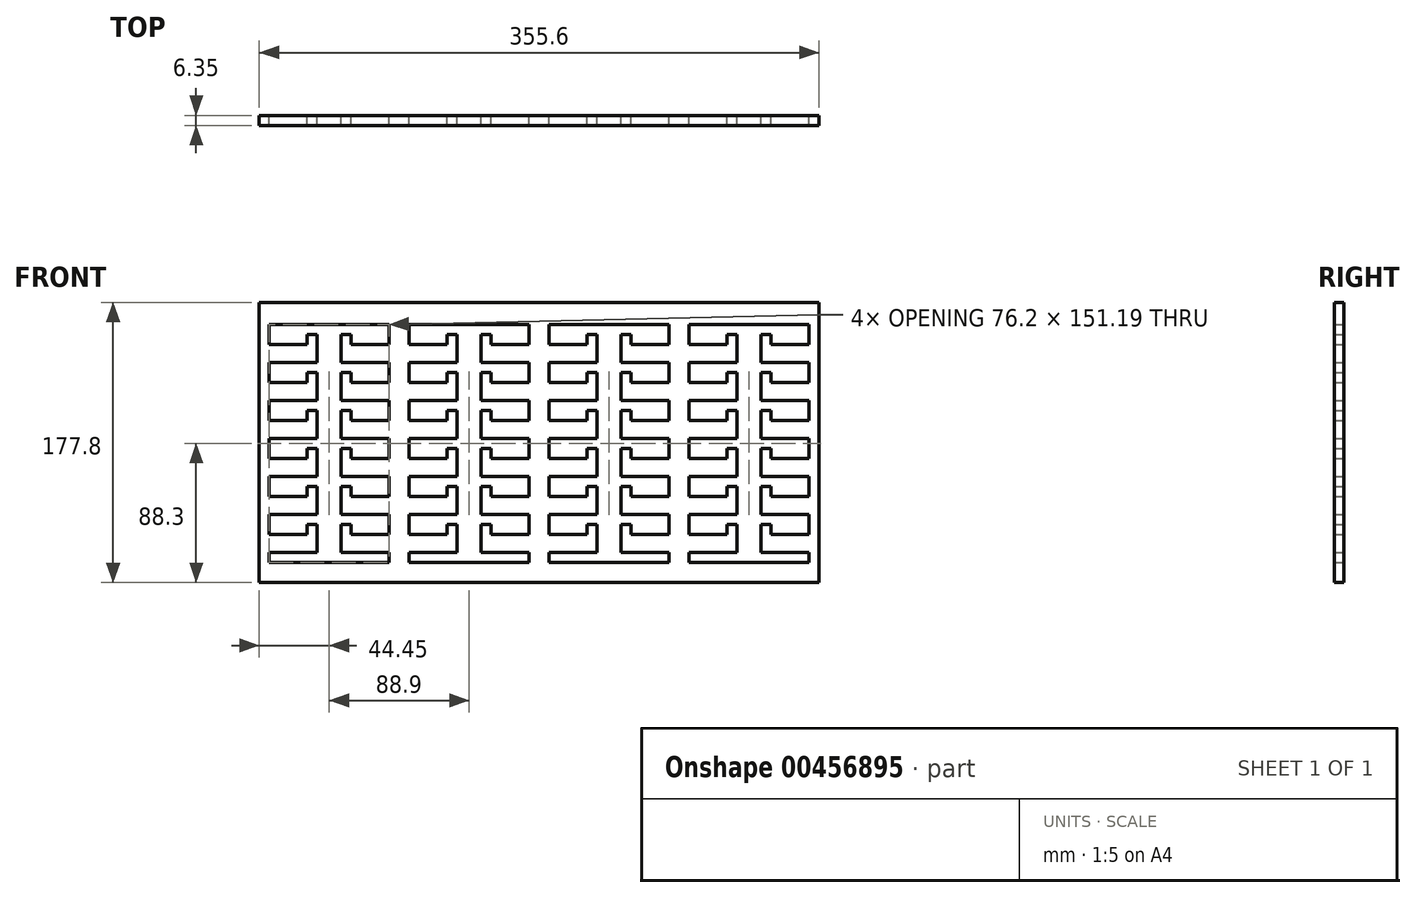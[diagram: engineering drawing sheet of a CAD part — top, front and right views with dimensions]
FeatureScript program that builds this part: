
annotation { "Feature Type Name" : "Feature", "Feature Type Description" : "" }
export const myFeature = defineFeature(function(context is Context, id is Id, definition is map)
    precondition{}
    {
        {
            var Q0;
            Q0=qCreatedBy(makeId("Front.planeOp"),FACE);
            var sketch = newSketch(context, id + "F0", { "sketchPlane" : qUnion([Q0])});
            skLineSegment(sketch, "E0", {"start": v(-97.96, -49.5) * mm, "end": v(-67.48, -49.5) * mm});
            skLineSegment(sketch, "E1", {"start": v(-67.48, -49.5) * mm, "end": v(-67.48, -31.72) * mm});
            skLineSegment(sketch, "E2", {"start": v(-67.48, -31.72) * mm, "end": v(-73.83, -31.72) * mm});
            skLineSegment(sketch, "E3", {"start": v(-73.83, -31.72) * mm, "end": v(-73.83, -38.07) * mm});
            skLineSegment(sketch, "E4", {"start": v(-73.83, -38.07) * mm, "end": v(-97.96, -38.07) * mm});
            skLineSegment(sketch, "E5", {"start": v(-97.96, -38.07) * mm, "end": v(-97.96, -25.37) * mm});
            skLineSegment(sketch, "E6", {"start": v(-97.96, -25.37) * mm, "end": v(-67.48, -25.37) * mm});
            skLineSegment(sketch, "E7", {"start": v(-67.48, -25.37) * mm, "end": v(-67.48, -7.6) * mm});
            skLineSegment(sketch, "E8", {"start": v(-67.48, -7.6) * mm, "end": v(-73.83, -7.6) * mm});
            skLineSegment(sketch, "E9", {"start": v(-73.83, -7.6) * mm, "end": v(-73.83, -13.94) * mm});
            skLineSegment(sketch, "E10", {"start": v(-73.83, -13.94) * mm, "end": v(-97.96, -13.94) * mm});
            skLineSegment(sketch, "E11", {"start": v(-97.96, -13.94) * mm, "end": v(-97.96, -1.24) * mm});
            skLineSegment(sketch, "E12", {"start": v(-97.96, -1.24) * mm, "end": v(-67.48, -1.24) * mm});
            skLineSegment(sketch, "E13", {"start": v(-67.48, -1.24) * mm, "end": v(-67.48, 16.54) * mm});
            skLineSegment(sketch, "E14", {"start": v(-67.48, 16.54) * mm, "end": v(-73.83, 16.54) * mm});
            skLineSegment(sketch, "E15", {"start": v(-73.83, 16.54) * mm, "end": v(-73.83, 10.19) * mm});
            skLineSegment(sketch, "E16", {"start": v(-73.83, 10.19) * mm, "end": v(-97.96, 10.19) * mm});
            skLineSegment(sketch, "E17", {"start": v(-97.96, 10.19) * mm, "end": v(-97.96, 22.89) * mm});
            skLineSegment(sketch, "E18", {"start": v(-97.96, 22.89) * mm, "end": v(-67.48, 22.89) * mm});
            skLineSegment(sketch, "E19", {"start": v(-67.48, 22.89) * mm, "end": v(-67.48, 40.67) * mm});
            skLineSegment(sketch, "E20", {"start": v(-67.48, 40.67) * mm, "end": v(-73.83, 40.67) * mm});
            skLineSegment(sketch, "E21", {"start": v(-73.83, 40.67) * mm, "end": v(-73.83, 34.32) * mm});
            skLineSegment(sketch, "E22", {"start": v(-73.83, 34.32) * mm, "end": v(-97.96, 34.32) * mm});
            skLineSegment(sketch, "E23", {"start": v(-97.96, 34.32) * mm, "end": v(-97.96, 47.02) * mm});
            skLineSegment(sketch, "E24", {"start": v(-97.96, 47.02) * mm, "end": v(-67.48, 47.02) * mm});
            skLineSegment(sketch, "E25", {"start": v(-67.48, 64.8) * mm, "end": v(-73.83, 64.8) * mm});
            skLineSegment(sketch, "E26", {"start": v(-73.83, 64.8) * mm, "end": v(-73.83, 58.45) * mm});
            skLineSegment(sketch, "E27", {"start": v(-73.83, 58.45) * mm, "end": v(-97.96, 58.45) * mm});
            skLineSegment(sketch, "E28", {"start": v(-97.96, 58.45) * mm, "end": v(-97.96, 71.15) * mm});
            skLineSegment(sketch, "E29", {"start": v(-21.76, -80.05) * mm, "end": v(-21.76, -73.63) * mm});
            skLineSegment(sketch, "E30", {"start": v(-21.76, -73.63) * mm, "end": v(-52.24, -73.63) * mm});
            skLineSegment(sketch, "E31", {"start": v(-52.24, -73.63) * mm, "end": v(-52.24, -55.85) * mm});
            skLineSegment(sketch, "E32", {"start": v(-52.24, -55.85) * mm, "end": v(-45.89, -55.85) * mm});
            skLineSegment(sketch, "E33", {"start": v(-45.89, -55.85) * mm, "end": v(-45.89, -62.2) * mm});
            skLineSegment(sketch, "E34", {"start": v(-45.89, -62.2) * mm, "end": v(-21.76, -62.2) * mm});
            skLineSegment(sketch, "E35", {"start": v(-21.76, -62.2) * mm, "end": v(-21.76, -49.5) * mm});
            skLineSegment(sketch, "E36", {"start": v(-21.76, -49.5) * mm, "end": v(-52.24, -49.5) * mm});
            skLineSegment(sketch, "E37", {"start": v(-52.24, -49.5) * mm, "end": v(-52.24, -31.72) * mm});
            skLineSegment(sketch, "E38", {"start": v(-52.24, -31.72) * mm, "end": v(-45.89, -31.72) * mm});
            skLineSegment(sketch, "E39", {"start": v(-45.89, -31.72) * mm, "end": v(-45.89, -38.07) * mm});
            skLineSegment(sketch, "E40", {"start": v(-45.89, -38.07) * mm, "end": v(-21.76, -38.07) * mm});
            skLineSegment(sketch, "E41", {"start": v(-21.76, -38.07) * mm, "end": v(-21.76, -25.37) * mm});
            skLineSegment(sketch, "E42", {"start": v(-21.76, -25.37) * mm, "end": v(-52.24, -25.37) * mm});
            skLineSegment(sketch, "E43", {"start": v(-52.24, -25.37) * mm, "end": v(-52.24, -7.6) * mm});
            skLineSegment(sketch, "E44", {"start": v(-52.24, -7.6) * mm, "end": v(-45.89, -7.6) * mm});
            skLineSegment(sketch, "E45", {"start": v(-45.89, -7.6) * mm, "end": v(-45.89, -13.94) * mm});
            skLineSegment(sketch, "E46", {"start": v(-45.89, -13.94) * mm, "end": v(-21.76, -13.94) * mm});
            skLineSegment(sketch, "E47", {"start": v(-21.76, -13.94) * mm, "end": v(-21.76, -1.24) * mm});
            skLineSegment(sketch, "E48", {"start": v(-21.76, -1.24) * mm, "end": v(-52.24, -1.24) * mm});
            skLineSegment(sketch, "E49", {"start": v(-52.24, -1.24) * mm, "end": v(-52.24, 16.54) * mm});
            skLineSegment(sketch, "E50", {"start": v(-52.24, 16.54) * mm, "end": v(-45.89, 16.54) * mm});
            skLineSegment(sketch, "E51", {"start": v(-45.89, 16.54) * mm, "end": v(-45.89, 10.19) * mm});
            skLineSegment(sketch, "E52", {"start": v(-45.89, 10.19) * mm, "end": v(-21.76, 10.19) * mm});
            skLineSegment(sketch, "E53", {"start": v(-21.76, 10.19) * mm, "end": v(-21.76, 22.89) * mm});
            skLineSegment(sketch, "E54", {"start": v(-21.76, 22.89) * mm, "end": v(-52.24, 22.89) * mm});
            skLineSegment(sketch, "E55", {"start": v(-52.24, 22.89) * mm, "end": v(-52.24, 40.67) * mm});
            skLineSegment(sketch, "E56", {"start": v(-52.24, 40.67) * mm, "end": v(-45.89, 40.67) * mm});
            skLineSegment(sketch, "E57", {"start": v(-45.89, 40.67) * mm, "end": v(-45.89, 34.32) * mm});
            skLineSegment(sketch, "E58", {"start": v(-45.89, 34.32) * mm, "end": v(-21.76, 34.32) * mm});
            skLineSegment(sketch, "E59", {"start": v(-21.76, 34.32) * mm, "end": v(-21.76, 47.02) * mm});
            skLineSegment(sketch, "E60", {"start": v(-21.76, 47.02) * mm, "end": v(-52.24, 47.02) * mm});
            skLineSegment(sketch, "E61", {"start": v(-52.24, 47.02) * mm, "end": v(-52.24, 64.8) * mm});
            skLineSegment(sketch, "E62", {"start": v(-52.24, 64.8) * mm, "end": v(-45.89, 64.8) * mm});
            skLineSegment(sketch, "E63", {"start": v(-45.89, 64.8) * mm, "end": v(-45.89, 58.45) * mm});
            skLineSegment(sketch, "E64", {"start": v(-45.89, 58.45) * mm, "end": v(-21.76, 58.45) * mm});
            skLineSegment(sketch, "E65", {"start": v(-21.76, 58.45) * mm, "end": v(-21.76, 71.15) * mm});
            skLineSegment(sketch, "E66", {"start": v(-67.48, 47.02) * mm, "end": v(-67.48, 64.8) * mm});
            skLineSegment(sketch, "E67", {"start": v(-67.48, -73.63) * mm, "end": v(-67.48, -55.85) * mm});
            skLineSegment(sketch, "E68", {"start": v(-73.83, -62.2) * mm, "end": v(-73.83, -55.85) * mm});
            skLineSegment(sketch, "E69", {"start": v(-73.83, -55.85) * mm, "end": v(-67.48, -55.85) * mm});
            skLineSegment(sketch, "E70", {"start": v(-67.48, -73.63) * mm, "end": v(-97.96, -73.63) * mm});
            skLineSegment(sketch, "E71", {"start": v(-97.96, -62.2) * mm, "end": v(-97.96, -49.5) * mm});
            skLineSegment(sketch, "E72", {"start": v(-97.96, -73.63) * mm, "end": v(-97.96, -80.05) * mm});
            skLineSegment(sketch, "E73", {"start": v(-97.96, -62.2) * mm, "end": v(-73.83, -62.2) * mm});
            skLineSegment(sketch, "E74", {"start": v(-97.96, -80.05) * mm, "end": v(-21.76, -80.05) * mm});
            skLineSegment(sketch, "E75", {"start": v(-97.96, 71.15) * mm, "end": v(-21.76, 71.15) * mm});
            skPoint(sketch, "E76", {"position": v(-59.86, 71.15) * mm});
            skPoint(sketch, "E77", {"position": v(-59.86, -80.05) * mm});
            skLineSegment(sketch, "E78", {"start": v(-186.86, -49.5) * mm, "end": v(-156.38, -49.5) * mm});
            skLineSegment(sketch, "E79", {"start": v(-156.38, -49.5) * mm, "end": v(-156.38, -31.72) * mm});
            skLineSegment(sketch, "E80", {"start": v(-156.38, -31.72) * mm, "end": v(-162.73, -31.72) * mm});
            skLineSegment(sketch, "E81", {"start": v(-162.73, -31.72) * mm, "end": v(-162.73, -38.07) * mm});
            skLineSegment(sketch, "E82", {"start": v(-162.73, -38.07) * mm, "end": v(-186.86, -38.07) * mm});
            skLineSegment(sketch, "E83", {"start": v(-186.86, -38.07) * mm, "end": v(-186.86, -25.37) * mm});
            skLineSegment(sketch, "E84", {"start": v(-186.86, -25.37) * mm, "end": v(-156.38, -25.37) * mm});
            skLineSegment(sketch, "E85", {"start": v(-156.38, -25.37) * mm, "end": v(-156.38, -7.6) * mm});
            skLineSegment(sketch, "E86", {"start": v(-156.38, -7.6) * mm, "end": v(-162.73, -7.6) * mm});
            skLineSegment(sketch, "E87", {"start": v(-162.73, -7.6) * mm, "end": v(-162.73, -13.94) * mm});
            skLineSegment(sketch, "E88", {"start": v(-162.73, -13.94) * mm, "end": v(-186.86, -13.94) * mm});
            skLineSegment(sketch, "E89", {"start": v(-186.86, -13.94) * mm, "end": v(-186.86, -1.24) * mm});
            skLineSegment(sketch, "E90", {"start": v(-186.86, -1.24) * mm, "end": v(-156.38, -1.24) * mm});
            skLineSegment(sketch, "E91", {"start": v(-156.38, -1.24) * mm, "end": v(-156.38, 16.54) * mm});
            skLineSegment(sketch, "E92", {"start": v(-156.38, 16.54) * mm, "end": v(-162.73, 16.54) * mm});
            skLineSegment(sketch, "E93", {"start": v(-162.73, 16.54) * mm, "end": v(-162.73, 10.19) * mm});
            skLineSegment(sketch, "E94", {"start": v(-162.73, 10.19) * mm, "end": v(-186.86, 10.19) * mm});
            skLineSegment(sketch, "E95", {"start": v(-186.86, 10.19) * mm, "end": v(-186.86, 22.89) * mm});
            skLineSegment(sketch, "E96", {"start": v(-186.86, 22.89) * mm, "end": v(-156.38, 22.89) * mm});
            skLineSegment(sketch, "E97", {"start": v(-156.38, 22.89) * mm, "end": v(-156.38, 40.67) * mm});
            skLineSegment(sketch, "E98", {"start": v(-156.38, 40.67) * mm, "end": v(-162.73, 40.67) * mm});
            skLineSegment(sketch, "E99", {"start": v(-162.73, 40.67) * mm, "end": v(-162.73, 34.32) * mm});
            skLineSegment(sketch, "E100", {"start": v(-162.73, 34.32) * mm, "end": v(-186.86, 34.32) * mm});
            skLineSegment(sketch, "E101", {"start": v(-186.86, 34.32) * mm, "end": v(-186.86, 47.02) * mm});
            skLineSegment(sketch, "E102", {"start": v(-186.86, 47.02) * mm, "end": v(-156.38, 47.02) * mm});
            skLineSegment(sketch, "E103", {"start": v(-156.38, 64.8) * mm, "end": v(-162.73, 64.8) * mm});
            skLineSegment(sketch, "E104", {"start": v(-162.73, 64.8) * mm, "end": v(-162.73, 58.45) * mm});
            skLineSegment(sketch, "E105", {"start": v(-162.73, 58.45) * mm, "end": v(-186.86, 58.45) * mm});
            skLineSegment(sketch, "E106", {"start": v(-186.86, 58.45) * mm, "end": v(-186.86, 71.15) * mm});
            skLineSegment(sketch, "E107", {"start": v(-110.66, -80.05) * mm, "end": v(-110.66, -73.63) * mm});
            skLineSegment(sketch, "E108", {"start": v(-110.66, -73.63) * mm, "end": v(-141.14, -73.63) * mm});
            skLineSegment(sketch, "E109", {"start": v(-141.14, -73.63) * mm, "end": v(-141.14, -55.85) * mm});
            skLineSegment(sketch, "E110", {"start": v(-141.14, -55.85) * mm, "end": v(-134.79, -55.85) * mm});
            skLineSegment(sketch, "E111", {"start": v(-134.79, -55.85) * mm, "end": v(-134.79, -62.2) * mm});
            skLineSegment(sketch, "E112", {"start": v(-134.79, -62.2) * mm, "end": v(-110.66, -62.2) * mm});
            skLineSegment(sketch, "E113", {"start": v(-110.66, -62.2) * mm, "end": v(-110.66, -49.5) * mm});
            skLineSegment(sketch, "E114", {"start": v(-110.66, -49.5) * mm, "end": v(-141.14, -49.5) * mm});
            skLineSegment(sketch, "E115", {"start": v(-141.14, -49.5) * mm, "end": v(-141.14, -31.72) * mm});
            skLineSegment(sketch, "E116", {"start": v(-141.14, -31.72) * mm, "end": v(-134.79, -31.72) * mm});
            skLineSegment(sketch, "E117", {"start": v(-134.79, -31.72) * mm, "end": v(-134.79, -38.07) * mm});
            skLineSegment(sketch, "E118", {"start": v(-134.79, -38.07) * mm, "end": v(-110.66, -38.07) * mm});
            skLineSegment(sketch, "E119", {"start": v(-110.66, -38.07) * mm, "end": v(-110.66, -25.37) * mm});
            skLineSegment(sketch, "E120", {"start": v(-110.66, -25.37) * mm, "end": v(-141.14, -25.37) * mm});
            skLineSegment(sketch, "E121", {"start": v(-141.14, -25.37) * mm, "end": v(-141.14, -7.6) * mm});
            skLineSegment(sketch, "E122", {"start": v(-141.14, -7.6) * mm, "end": v(-134.79, -7.6) * mm});
            skLineSegment(sketch, "E123", {"start": v(-134.79, -7.6) * mm, "end": v(-134.79, -13.94) * mm});
            skLineSegment(sketch, "E124", {"start": v(-134.79, -13.94) * mm, "end": v(-110.66, -13.94) * mm});
            skLineSegment(sketch, "E125", {"start": v(-110.66, -13.94) * mm, "end": v(-110.66, -1.24) * mm});
            skLineSegment(sketch, "E126", {"start": v(-110.66, -1.24) * mm, "end": v(-141.14, -1.24) * mm});
            skLineSegment(sketch, "E127", {"start": v(-141.14, -1.24) * mm, "end": v(-141.14, 16.54) * mm});
            skLineSegment(sketch, "E128", {"start": v(-141.14, 16.54) * mm, "end": v(-134.79, 16.54) * mm});
            skLineSegment(sketch, "E129", {"start": v(-134.79, 16.54) * mm, "end": v(-134.79, 10.19) * mm});
            skLineSegment(sketch, "E130", {"start": v(-134.79, 10.19) * mm, "end": v(-110.66, 10.19) * mm});
            skLineSegment(sketch, "E131", {"start": v(-110.66, 10.19) * mm, "end": v(-110.66, 22.89) * mm});
            skLineSegment(sketch, "E132", {"start": v(-110.66, 22.89) * mm, "end": v(-141.14, 22.89) * mm});
            skLineSegment(sketch, "E133", {"start": v(-141.14, 22.89) * mm, "end": v(-141.14, 40.67) * mm});
            skLineSegment(sketch, "E134", {"start": v(-141.14, 40.67) * mm, "end": v(-134.79, 40.67) * mm});
            skLineSegment(sketch, "E135", {"start": v(-134.79, 40.67) * mm, "end": v(-134.79, 34.32) * mm});
            skLineSegment(sketch, "E136", {"start": v(-134.79, 34.32) * mm, "end": v(-110.66, 34.32) * mm});
            skLineSegment(sketch, "E137", {"start": v(-110.66, 34.32) * mm, "end": v(-110.66, 47.02) * mm});
            skLineSegment(sketch, "E138", {"start": v(-110.66, 47.02) * mm, "end": v(-141.14, 47.02) * mm});
            skLineSegment(sketch, "E139", {"start": v(-141.14, 47.02) * mm, "end": v(-141.14, 64.8) * mm});
            skLineSegment(sketch, "E140", {"start": v(-141.14, 64.8) * mm, "end": v(-134.79, 64.8) * mm});
            skLineSegment(sketch, "E141", {"start": v(-134.79, 64.8) * mm, "end": v(-134.79, 58.45) * mm});
            skLineSegment(sketch, "E142", {"start": v(-134.79, 58.45) * mm, "end": v(-110.66, 58.45) * mm});
            skLineSegment(sketch, "E143", {"start": v(-110.66, 58.45) * mm, "end": v(-110.66, 71.15) * mm});
            skLineSegment(sketch, "E144", {"start": v(-156.38, 47.02) * mm, "end": v(-156.38, 64.8) * mm});
            skLineSegment(sketch, "E145", {"start": v(-156.38, -73.63) * mm, "end": v(-156.38, -55.85) * mm});
            skLineSegment(sketch, "E146", {"start": v(-162.73, -62.2) * mm, "end": v(-162.73, -55.85) * mm});
            skLineSegment(sketch, "E147", {"start": v(-162.73, -55.85) * mm, "end": v(-156.38, -55.85) * mm});
            skLineSegment(sketch, "E148", {"start": v(-156.38, -73.63) * mm, "end": v(-186.86, -73.63) * mm});
            skLineSegment(sketch, "E149", {"start": v(-186.86, -62.2) * mm, "end": v(-186.86, -49.5) * mm});
            skLineSegment(sketch, "E150", {"start": v(-186.86, -73.63) * mm, "end": v(-186.86, -80.05) * mm});
            skLineSegment(sketch, "E151", {"start": v(-186.86, -62.2) * mm, "end": v(-162.73, -62.2) * mm});
            skLineSegment(sketch, "E152", {"start": v(-186.86, -80.05) * mm, "end": v(-110.66, -80.05) * mm});
            skLineSegment(sketch, "E153", {"start": v(-186.86, 71.15) * mm, "end": v(-110.66, 71.15) * mm});
            skPoint(sketch, "E154", {"position": v(-148.76, 71.15) * mm});
            skPoint(sketch, "E155", {"position": v(-148.76, -80.05) * mm});
            skLineSegment(sketch, "E156", {"start": v(-275.76, -49.5) * mm, "end": v(-245.28, -49.5) * mm});
            skLineSegment(sketch, "E157", {"start": v(-245.28, -49.5) * mm, "end": v(-245.28, -31.72) * mm});
            skLineSegment(sketch, "E158", {"start": v(-245.28, -31.72) * mm, "end": v(-251.63, -31.72) * mm});
            skLineSegment(sketch, "E159", {"start": v(-251.63, -31.72) * mm, "end": v(-251.63, -38.07) * mm});
            skLineSegment(sketch, "E160", {"start": v(-251.63, -38.07) * mm, "end": v(-275.76, -38.07) * mm});
            skLineSegment(sketch, "E161", {"start": v(-275.76, -38.07) * mm, "end": v(-275.76, -25.37) * mm});
            skLineSegment(sketch, "E162", {"start": v(-275.76, -25.37) * mm, "end": v(-245.28, -25.37) * mm});
            skLineSegment(sketch, "E163", {"start": v(-245.28, -25.37) * mm, "end": v(-245.28, -7.6) * mm});
            skLineSegment(sketch, "E164", {"start": v(-245.28, -7.6) * mm, "end": v(-251.63, -7.6) * mm});
            skLineSegment(sketch, "E165", {"start": v(-251.63, -7.6) * mm, "end": v(-251.63, -13.94) * mm});
            skLineSegment(sketch, "E166", {"start": v(-251.63, -13.94) * mm, "end": v(-275.76, -13.94) * mm});
            skLineSegment(sketch, "E167", {"start": v(-275.76, -13.94) * mm, "end": v(-275.76, -1.24) * mm});
            skLineSegment(sketch, "E168", {"start": v(-275.76, -1.24) * mm, "end": v(-245.28, -1.24) * mm});
            skLineSegment(sketch, "E169", {"start": v(-245.28, -1.24) * mm, "end": v(-245.28, 16.54) * mm});
            skLineSegment(sketch, "E170", {"start": v(-245.28, 16.54) * mm, "end": v(-251.63, 16.54) * mm});
            skLineSegment(sketch, "E171", {"start": v(-251.63, 16.54) * mm, "end": v(-251.63, 10.19) * mm});
            skLineSegment(sketch, "E172", {"start": v(-251.63, 10.19) * mm, "end": v(-275.76, 10.19) * mm});
            skLineSegment(sketch, "E173", {"start": v(-275.76, 10.19) * mm, "end": v(-275.76, 22.89) * mm});
            skLineSegment(sketch, "E174", {"start": v(-275.76, 22.89) * mm, "end": v(-245.28, 22.89) * mm});
            skLineSegment(sketch, "E175", {"start": v(-245.28, 22.89) * mm, "end": v(-245.28, 40.67) * mm});
            skLineSegment(sketch, "E176", {"start": v(-245.28, 40.67) * mm, "end": v(-251.63, 40.67) * mm});
            skLineSegment(sketch, "E177", {"start": v(-251.63, 40.67) * mm, "end": v(-251.63, 34.32) * mm});
            skLineSegment(sketch, "E178", {"start": v(-251.63, 34.32) * mm, "end": v(-275.76, 34.32) * mm});
            skLineSegment(sketch, "E179", {"start": v(-275.76, 34.32) * mm, "end": v(-275.76, 47.02) * mm});
            skLineSegment(sketch, "E180", {"start": v(-275.76, 47.02) * mm, "end": v(-245.28, 47.02) * mm});
            skLineSegment(sketch, "E181", {"start": v(-245.28, 64.8) * mm, "end": v(-251.63, 64.8) * mm});
            skLineSegment(sketch, "E182", {"start": v(-251.63, 64.8) * mm, "end": v(-251.63, 58.45) * mm});
            skLineSegment(sketch, "E183", {"start": v(-251.63, 58.45) * mm, "end": v(-275.76, 58.45) * mm});
            skLineSegment(sketch, "E184", {"start": v(-275.76, 58.45) * mm, "end": v(-275.76, 71.15) * mm});
            skLineSegment(sketch, "E185", {"start": v(-199.56, -80.05) * mm, "end": v(-199.56, -73.63) * mm});
            skLineSegment(sketch, "E186", {"start": v(-199.56, -73.63) * mm, "end": v(-230.04, -73.63) * mm});
            skLineSegment(sketch, "E187", {"start": v(-230.04, -73.63) * mm, "end": v(-230.04, -55.85) * mm});
            skLineSegment(sketch, "E188", {"start": v(-230.04, -55.85) * mm, "end": v(-223.69, -55.85) * mm});
            skLineSegment(sketch, "E189", {"start": v(-223.69, -55.85) * mm, "end": v(-223.69, -62.2) * mm});
            skLineSegment(sketch, "E190", {"start": v(-223.69, -62.2) * mm, "end": v(-199.56, -62.2) * mm});
            skLineSegment(sketch, "E191", {"start": v(-199.56, -62.2) * mm, "end": v(-199.56, -49.5) * mm});
            skLineSegment(sketch, "E192", {"start": v(-199.56, -49.5) * mm, "end": v(-230.04, -49.5) * mm});
            skLineSegment(sketch, "E193", {"start": v(-230.04, -49.5) * mm, "end": v(-230.04, -31.72) * mm});
            skLineSegment(sketch, "E194", {"start": v(-230.04, -31.72) * mm, "end": v(-223.69, -31.72) * mm});
            skLineSegment(sketch, "E195", {"start": v(-223.69, -31.72) * mm, "end": v(-223.69, -38.07) * mm});
            skLineSegment(sketch, "E196", {"start": v(-223.69, -38.07) * mm, "end": v(-199.56, -38.07) * mm});
            skLineSegment(sketch, "E197", {"start": v(-199.56, -38.07) * mm, "end": v(-199.56, -25.37) * mm});
            skLineSegment(sketch, "E198", {"start": v(-199.56, -25.37) * mm, "end": v(-230.04, -25.37) * mm});
            skLineSegment(sketch, "E199", {"start": v(-230.04, -25.37) * mm, "end": v(-230.04, -7.6) * mm});
            skLineSegment(sketch, "E200", {"start": v(-230.04, -7.6) * mm, "end": v(-223.69, -7.6) * mm});
            skLineSegment(sketch, "E201", {"start": v(-223.69, -7.6) * mm, "end": v(-223.69, -13.94) * mm});
            skLineSegment(sketch, "E202", {"start": v(-223.69, -13.94) * mm, "end": v(-199.56, -13.94) * mm});
            skLineSegment(sketch, "E203", {"start": v(-199.56, -13.94) * mm, "end": v(-199.56, -1.24) * mm});
            skLineSegment(sketch, "E204", {"start": v(-199.56, -1.24) * mm, "end": v(-230.04, -1.24) * mm});
            skLineSegment(sketch, "E205", {"start": v(-230.04, -1.24) * mm, "end": v(-230.04, 16.54) * mm});
            skLineSegment(sketch, "E206", {"start": v(-230.04, 16.54) * mm, "end": v(-223.69, 16.54) * mm});
            skLineSegment(sketch, "E207", {"start": v(-223.69, 16.54) * mm, "end": v(-223.69, 10.19) * mm});
            skLineSegment(sketch, "E208", {"start": v(-223.69, 10.19) * mm, "end": v(-199.56, 10.19) * mm});
            skLineSegment(sketch, "E209", {"start": v(-199.56, 10.19) * mm, "end": v(-199.56, 22.89) * mm});
            skLineSegment(sketch, "E210", {"start": v(-199.56, 22.89) * mm, "end": v(-230.04, 22.89) * mm});
            skLineSegment(sketch, "E211", {"start": v(-230.04, 22.89) * mm, "end": v(-230.04, 40.67) * mm});
            skLineSegment(sketch, "E212", {"start": v(-230.04, 40.67) * mm, "end": v(-223.69, 40.67) * mm});
            skLineSegment(sketch, "E213", {"start": v(-223.69, 40.67) * mm, "end": v(-223.69, 34.32) * mm});
            skLineSegment(sketch, "E214", {"start": v(-223.69, 34.32) * mm, "end": v(-199.56, 34.32) * mm});
            skLineSegment(sketch, "E215", {"start": v(-199.56, 34.32) * mm, "end": v(-199.56, 47.02) * mm});
            skLineSegment(sketch, "E216", {"start": v(-199.56, 47.02) * mm, "end": v(-230.04, 47.02) * mm});
            skLineSegment(sketch, "E217", {"start": v(-230.04, 47.02) * mm, "end": v(-230.04, 64.8) * mm});
            skLineSegment(sketch, "E218", {"start": v(-230.04, 64.8) * mm, "end": v(-223.69, 64.8) * mm});
            skLineSegment(sketch, "E219", {"start": v(-223.69, 64.8) * mm, "end": v(-223.69, 58.45) * mm});
            skLineSegment(sketch, "E220", {"start": v(-223.69, 58.45) * mm, "end": v(-199.56, 58.45) * mm});
            skLineSegment(sketch, "E221", {"start": v(-199.56, 58.45) * mm, "end": v(-199.56, 71.15) * mm});
            skLineSegment(sketch, "E222", {"start": v(-245.28, 47.02) * mm, "end": v(-245.28, 64.8) * mm});
            skLineSegment(sketch, "E223", {"start": v(-245.28, -73.63) * mm, "end": v(-245.28, -55.85) * mm});
            skLineSegment(sketch, "E224", {"start": v(-251.63, -62.2) * mm, "end": v(-251.63, -55.85) * mm});
            skLineSegment(sketch, "E225", {"start": v(-251.63, -55.85) * mm, "end": v(-245.28, -55.85) * mm});
            skLineSegment(sketch, "E226", {"start": v(-245.28, -73.63) * mm, "end": v(-275.76, -73.63) * mm});
            skLineSegment(sketch, "E227", {"start": v(-275.76, -62.2) * mm, "end": v(-275.76, -49.5) * mm});
            skLineSegment(sketch, "E228", {"start": v(-275.76, -73.63) * mm, "end": v(-275.76, -80.05) * mm});
            skLineSegment(sketch, "E229", {"start": v(-275.76, -62.2) * mm, "end": v(-251.63, -62.2) * mm});
            skLineSegment(sketch, "E230", {"start": v(-275.76, -80.05) * mm, "end": v(-199.56, -80.05) * mm});
            skLineSegment(sketch, "E231", {"start": v(-275.76, 71.15) * mm, "end": v(-199.56, 71.15) * mm});
            skPoint(sketch, "E232", {"position": v(-237.66, 71.15) * mm});
            skPoint(sketch, "E233", {"position": v(-237.66, -80.05) * mm});
            skLineSegment(sketch, "E234", {"start": v(-364.66, -49.5) * mm, "end": v(-334.18, -49.5) * mm});
            skLineSegment(sketch, "E235", {"start": v(-334.18, -49.5) * mm, "end": v(-334.18, -31.72) * mm});
            skLineSegment(sketch, "E236", {"start": v(-334.18, -31.72) * mm, "end": v(-340.53, -31.72) * mm});
            skLineSegment(sketch, "E237", {"start": v(-340.53, -31.72) * mm, "end": v(-340.53, -38.07) * mm});
            skLineSegment(sketch, "E238", {"start": v(-340.53, -38.07) * mm, "end": v(-364.66, -38.07) * mm});
            skLineSegment(sketch, "E239", {"start": v(-364.66, -38.07) * mm, "end": v(-364.66, -25.37) * mm});
            skLineSegment(sketch, "E240", {"start": v(-364.66, -25.37) * mm, "end": v(-334.18, -25.37) * mm});
            skLineSegment(sketch, "E241", {"start": v(-334.18, -25.37) * mm, "end": v(-334.18, -7.6) * mm});
            skLineSegment(sketch, "E242", {"start": v(-334.18, -7.6) * mm, "end": v(-340.53, -7.6) * mm});
            skLineSegment(sketch, "E243", {"start": v(-340.53, -7.6) * mm, "end": v(-340.53, -13.94) * mm});
            skLineSegment(sketch, "E244", {"start": v(-340.53, -13.94) * mm, "end": v(-364.66, -13.94) * mm});
            skLineSegment(sketch, "E245", {"start": v(-364.66, -13.94) * mm, "end": v(-364.66, -1.24) * mm});
            skLineSegment(sketch, "E246", {"start": v(-364.66, -1.24) * mm, "end": v(-334.18, -1.24) * mm});
            skLineSegment(sketch, "E247", {"start": v(-334.18, -1.24) * mm, "end": v(-334.18, 16.54) * mm});
            skLineSegment(sketch, "E248", {"start": v(-334.18, 16.54) * mm, "end": v(-340.53, 16.54) * mm});
            skLineSegment(sketch, "E249", {"start": v(-340.53, 16.54) * mm, "end": v(-340.53, 10.19) * mm});
            skLineSegment(sketch, "E250", {"start": v(-340.53, 10.19) * mm, "end": v(-364.66, 10.19) * mm});
            skLineSegment(sketch, "E251", {"start": v(-364.66, 10.19) * mm, "end": v(-364.66, 22.89) * mm});
            skLineSegment(sketch, "E252", {"start": v(-364.66, 22.89) * mm, "end": v(-334.18, 22.89) * mm});
            skLineSegment(sketch, "E253", {"start": v(-334.18, 22.89) * mm, "end": v(-334.18, 40.67) * mm});
            skLineSegment(sketch, "E254", {"start": v(-334.18, 40.67) * mm, "end": v(-340.53, 40.67) * mm});
            skLineSegment(sketch, "E255", {"start": v(-340.53, 40.67) * mm, "end": v(-340.53, 34.32) * mm});
            skLineSegment(sketch, "E256", {"start": v(-340.53, 34.32) * mm, "end": v(-364.66, 34.32) * mm});
            skLineSegment(sketch, "E257", {"start": v(-364.66, 34.32) * mm, "end": v(-364.66, 47.02) * mm});
            skLineSegment(sketch, "E258", {"start": v(-364.66, 47.02) * mm, "end": v(-334.18, 47.02) * mm});
            skLineSegment(sketch, "E259", {"start": v(-334.18, 64.8) * mm, "end": v(-340.53, 64.8) * mm});
            skLineSegment(sketch, "E260", {"start": v(-340.53, 64.8) * mm, "end": v(-340.53, 58.45) * mm});
            skLineSegment(sketch, "E261", {"start": v(-340.53, 58.45) * mm, "end": v(-364.66, 58.45) * mm});
            skLineSegment(sketch, "E262", {"start": v(-364.66, 58.45) * mm, "end": v(-364.66, 71.15) * mm});
            skLineSegment(sketch, "E263", {"start": v(-288.46, -80.05) * mm, "end": v(-288.46, -73.63) * mm});
            skLineSegment(sketch, "E264", {"start": v(-288.46, -73.63) * mm, "end": v(-318.94, -73.63) * mm});
            skLineSegment(sketch, "E265", {"start": v(-318.94, -73.63) * mm, "end": v(-318.94, -55.85) * mm});
            skLineSegment(sketch, "E266", {"start": v(-318.94, -55.85) * mm, "end": v(-312.59, -55.85) * mm});
            skLineSegment(sketch, "E267", {"start": v(-312.59, -55.85) * mm, "end": v(-312.59, -62.2) * mm});
            skLineSegment(sketch, "E268", {"start": v(-312.59, -62.2) * mm, "end": v(-288.46, -62.2) * mm});
            skLineSegment(sketch, "E269", {"start": v(-288.46, -62.2) * mm, "end": v(-288.46, -49.5) * mm});
            skLineSegment(sketch, "E270", {"start": v(-288.46, -49.5) * mm, "end": v(-318.94, -49.5) * mm});
            skLineSegment(sketch, "E271", {"start": v(-318.94, -49.5) * mm, "end": v(-318.94, -31.72) * mm});
            skLineSegment(sketch, "E272", {"start": v(-318.94, -31.72) * mm, "end": v(-312.59, -31.72) * mm});
            skLineSegment(sketch, "E273", {"start": v(-312.59, -31.72) * mm, "end": v(-312.59, -38.07) * mm});
            skLineSegment(sketch, "E274", {"start": v(-312.59, -38.07) * mm, "end": v(-288.46, -38.07) * mm});
            skLineSegment(sketch, "E275", {"start": v(-288.46, -38.07) * mm, "end": v(-288.46, -25.37) * mm});
            skLineSegment(sketch, "E276", {"start": v(-288.46, -25.37) * mm, "end": v(-318.94, -25.37) * mm});
            skLineSegment(sketch, "E277", {"start": v(-318.94, -25.37) * mm, "end": v(-318.94, -7.6) * mm});
            skLineSegment(sketch, "E278", {"start": v(-318.94, -7.6) * mm, "end": v(-312.59, -7.6) * mm});
            skLineSegment(sketch, "E279", {"start": v(-312.59, -7.6) * mm, "end": v(-312.59, -13.94) * mm});
            skLineSegment(sketch, "E280", {"start": v(-312.59, -13.94) * mm, "end": v(-288.46, -13.94) * mm});
            skLineSegment(sketch, "E281", {"start": v(-288.46, -13.94) * mm, "end": v(-288.46, -1.24) * mm});
            skLineSegment(sketch, "E282", {"start": v(-288.46, -1.24) * mm, "end": v(-318.94, -1.24) * mm});
            skLineSegment(sketch, "E283", {"start": v(-318.94, -1.24) * mm, "end": v(-318.94, 16.54) * mm});
            skLineSegment(sketch, "E284", {"start": v(-318.94, 16.54) * mm, "end": v(-312.59, 16.54) * mm});
            skLineSegment(sketch, "E285", {"start": v(-312.59, 16.54) * mm, "end": v(-312.59, 10.19) * mm});
            skLineSegment(sketch, "E286", {"start": v(-312.59, 10.19) * mm, "end": v(-288.46, 10.19) * mm});
            skLineSegment(sketch, "E287", {"start": v(-288.46, 10.19) * mm, "end": v(-288.46, 22.89) * mm});
            skLineSegment(sketch, "E288", {"start": v(-288.46, 22.89) * mm, "end": v(-318.94, 22.89) * mm});
            skLineSegment(sketch, "E289", {"start": v(-318.94, 22.89) * mm, "end": v(-318.94, 40.67) * mm});
            skLineSegment(sketch, "E290", {"start": v(-318.94, 40.67) * mm, "end": v(-312.59, 40.67) * mm});
            skLineSegment(sketch, "E291", {"start": v(-312.59, 40.67) * mm, "end": v(-312.59, 34.32) * mm});
            skLineSegment(sketch, "E292", {"start": v(-312.59, 34.32) * mm, "end": v(-288.46, 34.32) * mm});
            skLineSegment(sketch, "E293", {"start": v(-288.46, 34.32) * mm, "end": v(-288.46, 47.02) * mm});
            skLineSegment(sketch, "E294", {"start": v(-288.46, 47.02) * mm, "end": v(-318.94, 47.02) * mm});
            skLineSegment(sketch, "E295", {"start": v(-318.94, 47.02) * mm, "end": v(-318.94, 64.8) * mm});
            skLineSegment(sketch, "E296", {"start": v(-318.94, 64.8) * mm, "end": v(-312.59, 64.8) * mm});
            skLineSegment(sketch, "E297", {"start": v(-312.59, 64.8) * mm, "end": v(-312.59, 58.45) * mm});
            skLineSegment(sketch, "E298", {"start": v(-312.59, 58.45) * mm, "end": v(-288.46, 58.45) * mm});
            skLineSegment(sketch, "E299", {"start": v(-288.46, 58.45) * mm, "end": v(-288.46, 71.15) * mm});
            skLineSegment(sketch, "E300", {"start": v(-334.18, 47.02) * mm, "end": v(-334.18, 64.8) * mm});
            skLineSegment(sketch, "E301", {"start": v(-334.18, -73.63) * mm, "end": v(-334.18, -55.85) * mm});
            skLineSegment(sketch, "E302", {"start": v(-340.53, -62.2) * mm, "end": v(-340.53, -55.85) * mm});
            skLineSegment(sketch, "E303", {"start": v(-340.53, -55.85) * mm, "end": v(-334.18, -55.85) * mm});
            skLineSegment(sketch, "E304", {"start": v(-334.18, -73.63) * mm, "end": v(-364.66, -73.63) * mm});
            skLineSegment(sketch, "E305", {"start": v(-364.66, -62.2) * mm, "end": v(-364.66, -49.5) * mm});
            skLineSegment(sketch, "E306", {"start": v(-364.66, -73.63) * mm, "end": v(-364.66, -80.05) * mm});
            skLineSegment(sketch, "E307", {"start": v(-364.66, -62.2) * mm, "end": v(-340.53, -62.2) * mm});
            skLineSegment(sketch, "E308", {"start": v(-364.66, -80.05) * mm, "end": v(-288.46, -80.05) * mm});
            skLineSegment(sketch, "E309", {"start": v(-364.66, 71.15) * mm, "end": v(-288.46, 71.15) * mm});
            skPoint(sketch, "E310", {"position": v(-326.56, 71.15) * mm});
            skPoint(sketch, "E311", {"position": v(-326.56, -80.05) * mm});
            skLineSegment(sketch, "E312.bottom", {"start": v(-15.4, 85.05) * mm, "end": v(-371, 85.05) * mm});
            skLineSegment(sketch, "E312.top", {"start": v(-15.4, -92.75) * mm, "end": v(-371, -92.75) * mm});
            skLineSegment(sketch, "E312.left", {"start": v(-15.4, 85.05) * mm, "end": v(-15.4, -92.75) * mm});
            skLineSegment(sketch, "E312.right", {"start": v(-371, 85.05) * mm, "end": v(-371, -92.75) * mm});
            skPoint(sketch, "E313", {"position": v(-193.2, 85.05) * mm});
            skLineSegment(sketch, "E314", {"start": v(-199.56, 71.15) * mm, "end": v(-186.86, 71.15) * mm});
            skPoint(sketch, "E315", {"position": v(-193.2, 71.15) * mm});
            skSolve(sketch);
        }
        {
            var Q0;
            Q0=makeQuery(id+"F0.imprint","IMPRINT",FACE,{"disambiguationData":[TD([[makeQuery(id+"F0.imprint","IMPRINT",EDGE,{"derivedFrom":sQuery(id+"F0.wireOp",EDGE,"E0")}),1.0]])]});
            extrude(context, id + "F1", {"entities" : qUnion([Q0]), "depth" : 6.35 * mm});
        }
    });
